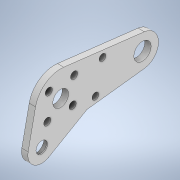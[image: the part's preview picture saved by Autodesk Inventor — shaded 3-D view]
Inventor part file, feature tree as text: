
AUTODESK INVENTOR PART (.ipt)
format: ipt  version: 2020 (Build 240168000, 168)  size: 266,240 bytes
history: native  units: mm
features: extrude x7, sketch x4, projected_geometry x3
ambient origin geometry x8: Origin, YZ Plane, XZ Plane, XY Plane, X Axis, Y Axis, Z Axis, Center Point
bodies: Body1 (feature_tree)
feature tree (14):
  extrude  "Выдавливание4"  Depth=18.6mm
  extrude  "Выдавливание5"  Depth=12.2mm
  extrude  "Выдавливание6"  Depth=9.7mm
  extrude  "Выдавливание7"  Depth=7.1mm
  sketch  "Эскиз7"
  extrude  "Выдавливание8"  Depth=38.82013mm
  extrude  "Выдавливание9"  Depth=38.8mm
  extrude  "Выдавливание10"  Depth=38.8mm
  sketch  "Эскиз4"
  projected_geometry  "Спроецированная петля3"
  sketch  "Эскиз5"
  sketch  "Эскиз6"
  projected_geometry  "Спроецированная петля4"
  projected_geometry  "Спроецированная петля5"
